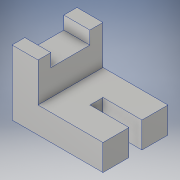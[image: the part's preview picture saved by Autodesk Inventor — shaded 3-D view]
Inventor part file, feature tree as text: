
AUTODESK INVENTOR PART (.ipt)
format: ipt  version: 2017 (Build 210142000, 142)  size: 120,320 bytes
history: native  units: in
note: dims shown in document units (in); Inventor stores cm internally (conversion verified against a paired STEP export)
features: extrude x3, sketch x3
ambient origin geometry x8: Origin, YZ Plane, XZ Plane, XY Plane, X Axis, Y Axis, Z Axis, Center Point
bodies: Solid1 (feature_tree)
feature tree (6):
  extrude  "Extrusion1"  Depth=0.5in
  extrude  "Extrusion2"  Depth=0.75in
  extrude  "Extrusion3"  Depth=0.25in
  sketch  "Sketch1"  dims[d0=1.75in d1=0.5in]
  sketch  "Sketch2"  dims[d2=1.25in d3=0.75in]
  sketch  "Sketch4"  dims[d4=1.25in d5=0.0in d6=0.25in d7=0.75in d8=0.25in d9=0.0in d10=0.5in d11=0.75in d12=0.25in d13=0.75in d14=0.0in]
